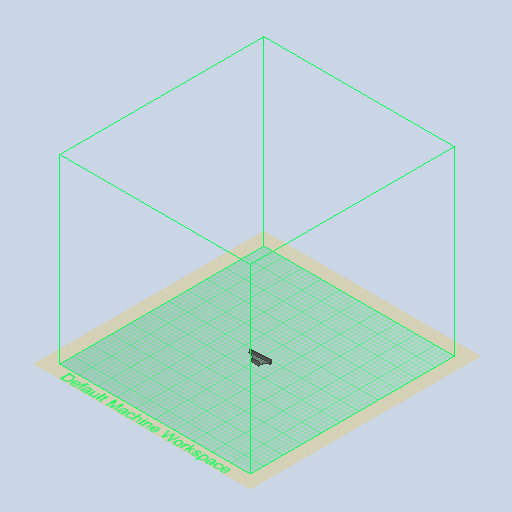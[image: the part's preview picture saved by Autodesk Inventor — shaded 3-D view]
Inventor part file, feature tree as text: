
AUTODESK INVENTOR PART (.ipt)
format: ipt  version: 2022 (Build 260153000, 153)  size: 321,024 bytes
history: native  units: in
note: dims shown in document units (in); Inventor stores cm internally (conversion verified against a paired STEP export)
features: extrude x2, sketch x2, other x1
ambient origin geometry x8: Origin, YZ Plane, XZ Plane, XY Plane, X Axis, Y Axis, Z Axis, Center Point
bodies: Body1 (feature_tree)
feature tree (5):
  other  "Sólido1"
  extrude  "Extrusión1"  Depth=0.2559in
  extrude  "Extrusión2"  Depth=0.0787in
  sketch  "Boceto1"  dims[d19=0.2559in d20=0.0in d27=0.1378in d31=0.128in]
  sketch  "Boceto2"  dims[d38=0.0394in d39=0.0in d40=0.0787in d41=0.0787in]
